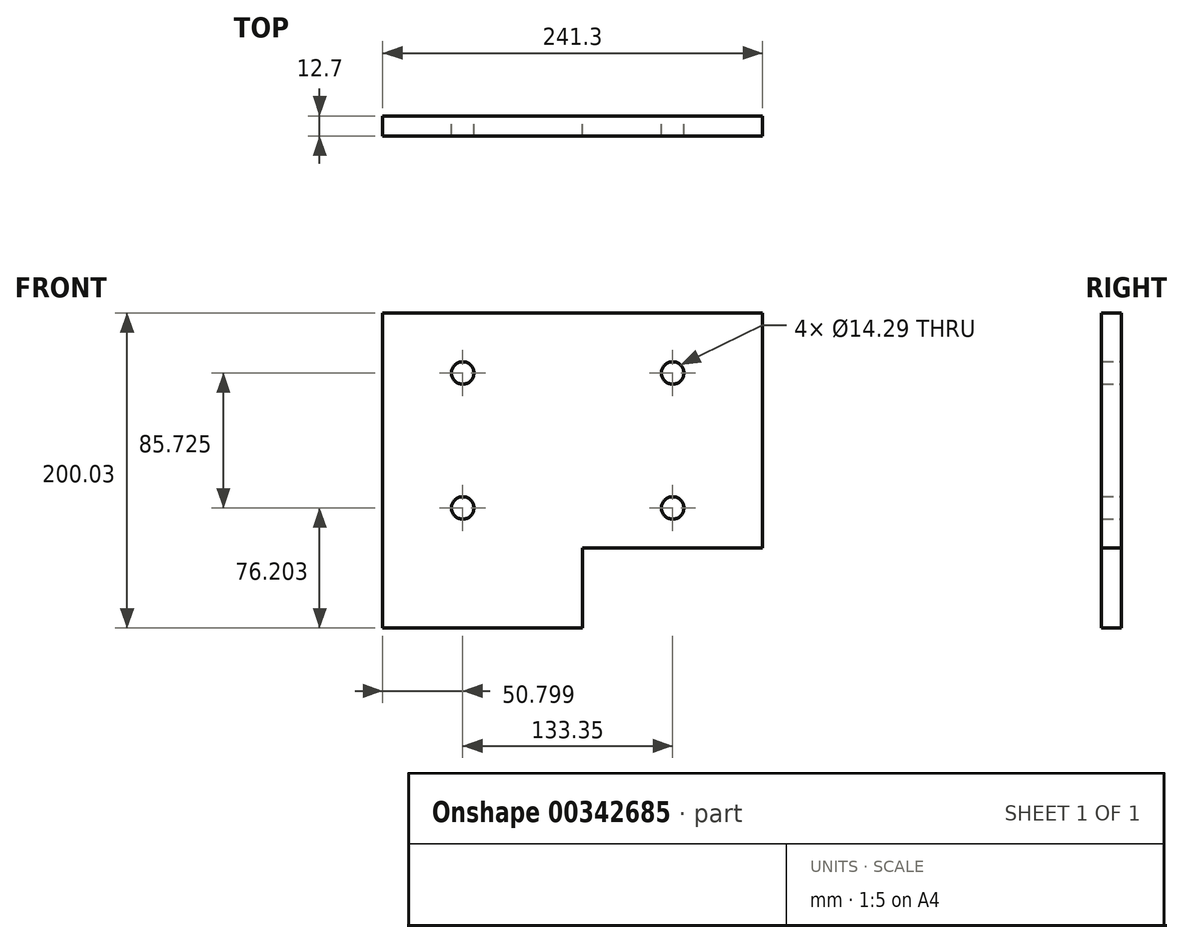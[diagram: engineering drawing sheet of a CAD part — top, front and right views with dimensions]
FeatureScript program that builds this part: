
annotation { "Feature Type Name" : "Feature", "Feature Type Description" : "" }
export const myFeature = defineFeature(function(context is Context, id is Id, definition is map)
    precondition{}
    {
        {
            var Q0;
            Q0=qCreatedBy(makeId("Front.planeOp"),FACE);
            var sketch = newSketch(context, id + "F0", { "sketchPlane" : qUnion([Q0])});
            skLineSegment(sketch, "E0.bottom", {"start": v(-120.74, 134.1) * mm, "end": v(120.56, 134.1) * mm});
            skLineSegment(sketch, "E0.top", {"start": v(-120.74, -65.92) * mm, "end": v(6.26, -65.92) * mm});
            skLineSegment(sketch, "E0.left", {"start": v(-120.74, 134.1) * mm, "end": v(-120.74, -65.92) * mm});
            skLineSegment(sketch, "E0.right", {"start": v(120.56, 134.1) * mm, "end": v(120.56, -15.12) * mm});
            skCircle(sketch, "E1", {"center": v(-69.94, 10.28) * mm, "radius": 7.14 * mm});
            skCircle(sketch, "E2.0.1.0", {"center": v(-69.94, 96) * mm, "radius": 7.14 * mm});
            skCircle(sketch, "E2.1.0.0", {"center": v(63.4, 10.28) * mm, "radius": 7.14 * mm});
            skCircle(sketch, "E2.1.1.0", {"center": v(63.4, 96) * mm, "radius": 7.14 * mm});
            skLineSegment(sketch, "E2.direction1", {"start": v(-69.94, 10.28) * mm, "end": v(63.4, 10.28) * mm, "construction": true});
            skLineSegment(sketch, "E2.direction2", {"start": v(-69.94, 10.28) * mm, "end": v(-69.94, 96) * mm, "construction": true});
            skLineSegment(sketch, "E3.top", {"start": v(120.56, -15.12) * mm, "end": v(6.26, -15.12) * mm});
            skLineSegment(sketch, "E3.right", {"start": v(6.26, -65.92) * mm, "end": v(6.26, -15.12) * mm});
            skSolve(sketch);
        }
        {
            var Q0;
            Q0=makeQuery(id+"F0.imprint","IMPRINT",FACE,{"disambiguationData":[TD([[makeQuery(id+"F0.imprint","IMPRINT",EDGE,{"derivedFrom":sQuery(id+"F0.wireOp",EDGE,"E0.bottom")}),-1.0]])]});
            extrude(context, id + "F1", {"entities" : qUnion([Q0]), "depth" : 12.7 * mm});
        }
    });
